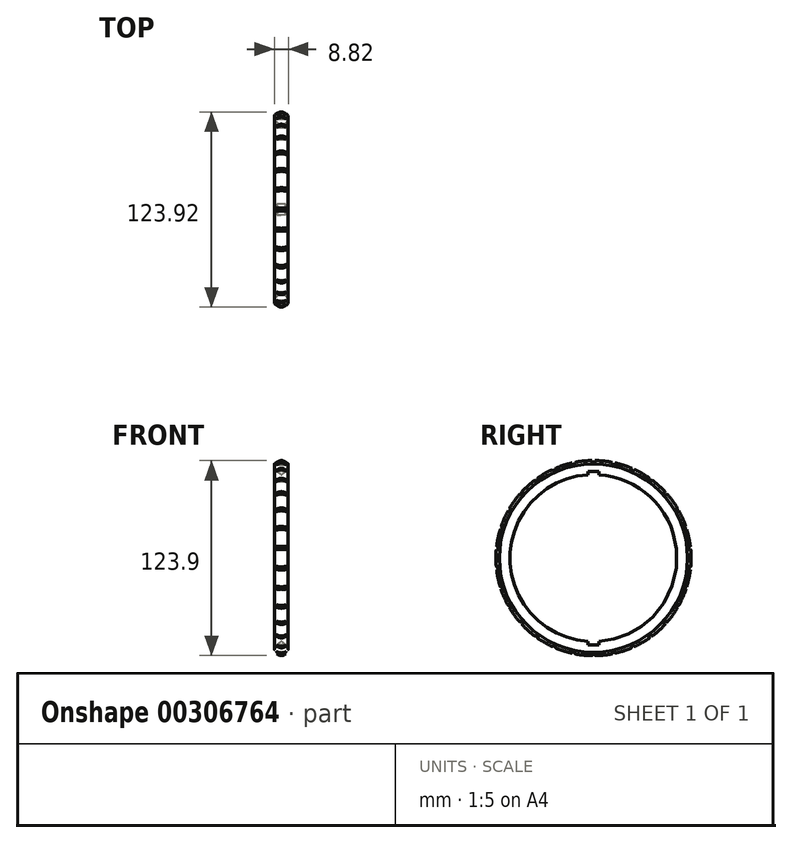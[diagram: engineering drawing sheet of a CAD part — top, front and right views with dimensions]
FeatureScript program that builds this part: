
annotation { "Feature Type Name" : "Feature", "Feature Type Description" : "" }
export const myFeature = defineFeature(function(context is Context, id is Id, definition is map)
    precondition{}
    {
        {
            var Q0;
            Q0=qCreatedBy(makeId("Top.planeOp"),FACE);
            var sketch = newSketch(context, id + "F0", { "sketchPlane" : qUnion([Q0])});
            skLineSegment(sketch, "E0", {"start": v(0, 0) * mm, "end": v(0, -12.81) * mm, "construction": true});
            skLineSegment(sketch, "E1", {"start": v(-4.23, -56.43) * mm, "end": v(-0.32, -53.16) * mm});
            skLineSegment(sketch, "E2", {"start": v(0.32, -53.16) * mm, "end": v(4.23, -56.43) * mm});
            skPoint(sketch, "E3.orphan", {"position": v(-5.08, -57.15) * mm});
            skPoint(sketch, "E4.orphan", {"position": v(5.08, -57.15) * mm});
            skLineSegment(sketch, "E5", {"start": v(-4.4, -56.82) * mm, "end": v(-4.4, -59.82) * mm});
            skLineSegment(sketch, "E6", {"start": v(4.4, -59.82) * mm, "end": v(4.4, -56.82) * mm});
            skPoint(sketch, "E7.visualSharp", {"position": v(-4.4, -56.58) * mm});
            skArc(sketch, "E7.filletArc", {"start": v(-4.23, -56.43) * mm, "mid": v(-4.36, -56.6) * mm, "end": v(-4.4, -56.82) * mm});
            skPoint(sketch, "E8.visualSharp", {"position": v(4.4, -56.58) * mm});
            skArc(sketch, "E8.filletArc", {"start": v(4.4, -56.82) * mm, "mid": v(4.36, -56.6) * mm, "end": v(4.23, -56.43) * mm});
            skPoint(sketch, "E9.visualSharp", {"position": v(0, -52.89) * mm});
            skArc(sketch, "E9.filletArc", {"start": v(0.32, -53.16) * mm, "mid": v(0, -53.04) * mm, "end": v(-0.32, -53.16) * mm});
            skLineSegment(sketch, "E10", {"start": v(0, 0) * mm, "end": v(13.38, 0) * mm, "construction": true});
            skFitSpline(sketch, "E11", {"points": [v(-4.4, -59.82) * mm, v(0, -61.96) * mm, v(4.4, -59.82) * mm], "startDerivative": vector(8.81, -6.43) * mm, "endDerivative": vector(8.81, 6.43) * mm});
            skSolve(sketch);
        }
        {
            var Q0;
            Q0=makeQuery(id+"F0.imprint","IMPRINT",FACE,{"disambiguationData":[TD([[makeQuery(id+"F0.imprint","IMPRINT",EDGE,{"derivedFrom":sQuery(id+"F0.wireOp",EDGE,"E1")}),-1.0]])]});
            var Q1;
            Q1=sQuery(id+"F0.wireOp",EDGE,"E10");
            revolve(context, id + "F1", {"entities" : qUnion([Q0]), "axis" : qUnion([Q1]), "revolveType" : RevolveType.FULL});
        }
        {
            var Q0;
            Q0=qCreatedBy(makeId("Top.planeOp"),FACE);
            var sketch = newSketch(context, id + "F2", { "sketchPlane" : qUnion([Q0])});
            skLineSegment(sketch, "E12.bottom", {"start": v(3.5, 3.5) * mm, "end": v(-3.5, 3.5) * mm});
            skLineSegment(sketch, "E12.top", {"start": v(3.5, -3.5) * mm, "end": v(-3.5, -3.5) * mm});
            skLineSegment(sketch, "E12.left", {"start": v(3.5, 3.5) * mm, "end": v(3.5, -3.5) * mm});
            skLineSegment(sketch, "E12.right", {"start": v(-3.5, 3.5) * mm, "end": v(-3.5, -3.5) * mm});
            skPoint(sketch, "E12.middle", {"position": v(0, 0) * mm});
            skSolve(sketch);
        }
        {
            var Q0;
            Q0 = qSketchRegion(id + "F2", true);
            extrude(context, id + "F3", {"entities" : qUnion([Q0]), "operationType" : NewBodyOperationType.REMOVE, "endBound" : BoundingType.SYMMETRIC, "oppositeDirection" : true, "depth" : 110 * mm});
        }
        {
            var Q0;
            Q0=qCreatedBy(makeId("Right.planeOp"),FACE);
            var sketch = newSketch(context, id + "F4", { "sketchPlane" : qUnion([Q0])});
            skLineSegment(sketch, "E13", {"start": v(0, 60.84) * mm, "end": v(-0.97, 60.84) * mm});
            skLineSegment(sketch, "E14", {"start": v(-0.97, 60.84) * mm, "end": v(-0.97, 62.61) * mm});
            skLineSegment(sketch, "E15", {"start": v(-0.97, 62.61) * mm, "end": v(0, 62.61) * mm});
            skLineSegment(sketch, "E16", {"start": v(0, 62.61) * mm, "end": v(0, 60.46) * mm, "construction": true});
            skLineSegment(sketch, "E17.MirrorCS", {"start": v(0.97, 62.61) * mm, "end": v(0, 62.61) * mm});
            skLineSegment(sketch, "E18.MirrorCS", {"start": v(0.97, 60.84) * mm, "end": v(0.97, 62.61) * mm});
            skLineSegment(sketch, "E19.MirrorCS", {"start": v(0, 60.84) * mm, "end": v(0.97, 60.84) * mm});
            skLineSegment(sketch, "E20.1.0", {"start": v(-12.65, 59.5) * mm, "end": v(-13.6, 59.3) * mm});
            skLineSegment(sketch, "E20.1.1", {"start": v(-11.7, 59.7) * mm, "end": v(-12.07, 61.45) * mm});
            skLineSegment(sketch, "E20.1.2", {"start": v(-12.65, 59.5) * mm, "end": v(-11.7, 59.7) * mm});
            skLineSegment(sketch, "E20.1.3", {"start": v(-12.07, 61.45) * mm, "end": v(-13.02, 61.25) * mm});
            skLineSegment(sketch, "E20.1.4", {"start": v(-13.97, 61.04) * mm, "end": v(-13.02, 61.25) * mm});
            skLineSegment(sketch, "E20.1.5", {"start": v(-13.6, 59.3) * mm, "end": v(-13.97, 61.04) * mm});
            skLineSegment(sketch, "E20.2.0", {"start": v(-24.74, 55.58) * mm, "end": v(-25.63, 55.18) * mm});
            skLineSegment(sketch, "E20.2.1", {"start": v(-23.86, 55.97) * mm, "end": v(-24.58, 57.6) * mm});
            skLineSegment(sketch, "E20.2.2", {"start": v(-24.74, 55.58) * mm, "end": v(-23.86, 55.97) * mm});
            skLineSegment(sketch, "E20.2.3", {"start": v(-24.58, 57.6) * mm, "end": v(-25.47, 57.2) * mm});
            skLineSegment(sketch, "E20.2.4", {"start": v(-26.36, 56.8) * mm, "end": v(-25.47, 57.2) * mm});
            skLineSegment(sketch, "E20.2.5", {"start": v(-25.63, 55.18) * mm, "end": v(-26.36, 56.8) * mm});
            skLineSegment(sketch, "E20.3.0", {"start": v(-35.76, 49.22) * mm, "end": v(-36.55, 48.65) * mm});
            skLineSegment(sketch, "E20.3.1", {"start": v(-34.97, 49.79) * mm, "end": v(-36.02, 51.23) * mm});
            skLineSegment(sketch, "E20.3.2", {"start": v(-35.76, 49.22) * mm, "end": v(-34.97, 49.79) * mm});
            skLineSegment(sketch, "E20.3.3", {"start": v(-36.02, 51.23) * mm, "end": v(-36.8, 50.66) * mm});
            skLineSegment(sketch, "E20.3.4", {"start": v(-37.59, 50.08) * mm, "end": v(-36.8, 50.66) * mm});
            skLineSegment(sketch, "E20.3.5", {"start": v(-36.55, 48.65) * mm, "end": v(-37.59, 50.08) * mm});
            skLineSegment(sketch, "E20.4.0", {"start": v(-45.21, 40.7) * mm, "end": v(-45.86, 39.99) * mm});
            skLineSegment(sketch, "E20.4.1", {"start": v(-44.56, 41.43) * mm, "end": v(-45.88, 42.62) * mm});
            skLineSegment(sketch, "E20.4.2", {"start": v(-45.21, 40.7) * mm, "end": v(-44.56, 41.43) * mm});
            skLineSegment(sketch, "E20.4.3", {"start": v(-45.88, 42.62) * mm, "end": v(-46.53, 41.9) * mm});
            skLineSegment(sketch, "E20.4.4", {"start": v(-47.18, 41.17) * mm, "end": v(-46.53, 41.9) * mm});
            skLineSegment(sketch, "E20.4.5", {"start": v(-45.86, 39.99) * mm, "end": v(-47.18, 41.17) * mm});
            skLineSegment(sketch, "E20.5.0", {"start": v(-52.69, 30.42) * mm, "end": v(-53.17, 29.58) * mm});
            skLineSegment(sketch, "E20.5.1", {"start": v(-52.2, 31.26) * mm, "end": v(-53.74, 32.15) * mm});
            skLineSegment(sketch, "E20.5.2", {"start": v(-52.69, 30.42) * mm, "end": v(-52.2, 31.26) * mm});
            skLineSegment(sketch, "E20.5.3", {"start": v(-53.74, 32.15) * mm, "end": v(-54.22, 31.3) * mm});
            skLineSegment(sketch, "E20.5.4", {"start": v(-54.71, 30.46) * mm, "end": v(-54.22, 31.3) * mm});
            skLineSegment(sketch, "E20.5.5", {"start": v(-53.17, 29.58) * mm, "end": v(-54.71, 30.46) * mm});
            skLineSegment(sketch, "E20.6.0", {"start": v(-57.86, 18.8) * mm, "end": v(-58.16, 17.88) * mm});
            skLineSegment(sketch, "E20.6.1", {"start": v(-57.56, 19.72) * mm, "end": v(-59.25, 20.27) * mm});
            skLineSegment(sketch, "E20.6.2", {"start": v(-57.86, 18.8) * mm, "end": v(-57.56, 19.72) * mm});
            skLineSegment(sketch, "E20.6.3", {"start": v(-59.25, 20.27) * mm, "end": v(-59.55, 19.35) * mm});
            skLineSegment(sketch, "E20.6.4", {"start": v(-59.85, 18.42) * mm, "end": v(-59.55, 19.35) * mm});
            skLineSegment(sketch, "E20.6.5", {"start": v(-58.16, 17.88) * mm, "end": v(-59.85, 18.42) * mm});
            skLineSegment(sketch, "E20.7.0", {"start": v(-60.5, 6.36) * mm, "end": v(-60.6, 5.4) * mm});
            skLineSegment(sketch, "E20.7.1", {"start": v(-60.4, 7.33) * mm, "end": v(-62.17, 7.51) * mm});
            skLineSegment(sketch, "E20.7.2", {"start": v(-60.5, 6.36) * mm, "end": v(-60.4, 7.33) * mm});
            skLineSegment(sketch, "E20.7.3", {"start": v(-62.17, 7.51) * mm, "end": v(-62.27, 6.54) * mm});
            skLineSegment(sketch, "E20.7.4", {"start": v(-62.37, 5.58) * mm, "end": v(-62.27, 6.54) * mm});
            skLineSegment(sketch, "E20.7.5", {"start": v(-60.6, 5.4) * mm, "end": v(-62.37, 5.58) * mm});
            skLineSegment(sketch, "E20.8.0", {"start": v(-60.5, -6.36) * mm, "end": v(-60.4, -7.33) * mm});
            skLineSegment(sketch, "E20.8.1", {"start": v(-60.6, -5.4) * mm, "end": v(-62.37, -5.58) * mm});
            skLineSegment(sketch, "E20.8.2", {"start": v(-60.5, -6.36) * mm, "end": v(-60.6, -5.4) * mm});
            skLineSegment(sketch, "E20.8.3", {"start": v(-62.37, -5.58) * mm, "end": v(-62.27, -6.54) * mm});
            skLineSegment(sketch, "E20.8.4", {"start": v(-62.17, -7.51) * mm, "end": v(-62.27, -6.54) * mm});
            skLineSegment(sketch, "E20.8.5", {"start": v(-60.4, -7.33) * mm, "end": v(-62.17, -7.51) * mm});
            skLineSegment(sketch, "E20.9.0", {"start": v(-57.86, -18.8) * mm, "end": v(-57.56, -19.72) * mm});
            skLineSegment(sketch, "E20.9.1", {"start": v(-58.16, -17.88) * mm, "end": v(-59.85, -18.42) * mm});
            skLineSegment(sketch, "E20.9.2", {"start": v(-57.86, -18.8) * mm, "end": v(-58.16, -17.88) * mm});
            skLineSegment(sketch, "E20.9.3", {"start": v(-59.85, -18.42) * mm, "end": v(-59.55, -19.35) * mm});
            skLineSegment(sketch, "E20.9.4", {"start": v(-59.25, -20.27) * mm, "end": v(-59.55, -19.35) * mm});
            skLineSegment(sketch, "E20.9.5", {"start": v(-57.56, -19.72) * mm, "end": v(-59.25, -20.27) * mm});
            skLineSegment(sketch, "E20.10.0", {"start": v(-52.69, -30.42) * mm, "end": v(-52.2, -31.26) * mm});
            skLineSegment(sketch, "E20.10.1", {"start": v(-53.17, -29.58) * mm, "end": v(-54.71, -30.46) * mm});
            skLineSegment(sketch, "E20.10.2", {"start": v(-52.69, -30.42) * mm, "end": v(-53.17, -29.58) * mm});
            skLineSegment(sketch, "E20.10.3", {"start": v(-54.71, -30.46) * mm, "end": v(-54.22, -31.3) * mm});
            skLineSegment(sketch, "E20.10.4", {"start": v(-53.74, -32.15) * mm, "end": v(-54.22, -31.3) * mm});
            skLineSegment(sketch, "E20.10.5", {"start": v(-52.2, -31.26) * mm, "end": v(-53.74, -32.15) * mm});
            skLineSegment(sketch, "E20.11.0", {"start": v(-45.21, -40.7) * mm, "end": v(-44.56, -41.43) * mm});
            skLineSegment(sketch, "E20.11.1", {"start": v(-45.86, -39.99) * mm, "end": v(-47.18, -41.17) * mm});
            skLineSegment(sketch, "E20.11.2", {"start": v(-45.21, -40.7) * mm, "end": v(-45.86, -39.99) * mm});
            skLineSegment(sketch, "E20.11.3", {"start": v(-47.18, -41.17) * mm, "end": v(-46.53, -41.9) * mm});
            skLineSegment(sketch, "E20.11.4", {"start": v(-45.88, -42.62) * mm, "end": v(-46.53, -41.9) * mm});
            skLineSegment(sketch, "E20.11.5", {"start": v(-44.56, -41.43) * mm, "end": v(-45.88, -42.62) * mm});
            skLineSegment(sketch, "E20.12.0", {"start": v(-35.76, -49.22) * mm, "end": v(-34.97, -49.79) * mm});
            skLineSegment(sketch, "E20.12.1", {"start": v(-36.55, -48.65) * mm, "end": v(-37.59, -50.08) * mm});
            skLineSegment(sketch, "E20.12.2", {"start": v(-35.76, -49.22) * mm, "end": v(-36.55, -48.65) * mm});
            skLineSegment(sketch, "E20.12.3", {"start": v(-37.59, -50.08) * mm, "end": v(-36.8, -50.66) * mm});
            skLineSegment(sketch, "E20.12.4", {"start": v(-36.02, -51.23) * mm, "end": v(-36.8, -50.66) * mm});
            skLineSegment(sketch, "E20.12.5", {"start": v(-34.97, -49.79) * mm, "end": v(-36.02, -51.23) * mm});
            skLineSegment(sketch, "E20.13.0", {"start": v(-24.74, -55.58) * mm, "end": v(-23.86, -55.97) * mm});
            skLineSegment(sketch, "E20.13.1", {"start": v(-25.63, -55.18) * mm, "end": v(-26.36, -56.8) * mm});
            skLineSegment(sketch, "E20.13.2", {"start": v(-24.74, -55.58) * mm, "end": v(-25.63, -55.18) * mm});
            skLineSegment(sketch, "E20.13.3", {"start": v(-26.36, -56.8) * mm, "end": v(-25.47, -57.2) * mm});
            skLineSegment(sketch, "E20.13.4", {"start": v(-24.58, -57.6) * mm, "end": v(-25.47, -57.2) * mm});
            skLineSegment(sketch, "E20.13.5", {"start": v(-23.86, -55.97) * mm, "end": v(-24.58, -57.6) * mm});
            skLineSegment(sketch, "E20.14.0", {"start": v(-12.65, -59.5) * mm, "end": v(-11.7, -59.7) * mm});
            skLineSegment(sketch, "E20.14.1", {"start": v(-13.6, -59.3) * mm, "end": v(-13.97, -61.04) * mm});
            skLineSegment(sketch, "E20.14.2", {"start": v(-12.65, -59.5) * mm, "end": v(-13.6, -59.3) * mm});
            skLineSegment(sketch, "E20.14.3", {"start": v(-13.97, -61.04) * mm, "end": v(-13.02, -61.25) * mm});
            skLineSegment(sketch, "E20.14.4", {"start": v(-12.07, -61.45) * mm, "end": v(-13.02, -61.25) * mm});
            skLineSegment(sketch, "E20.14.5", {"start": v(-11.7, -59.7) * mm, "end": v(-12.07, -61.45) * mm});
            skLineSegment(sketch, "E20.15.0", {"start": v(0, -60.84) * mm, "end": v(0.97, -60.84) * mm});
            skLineSegment(sketch, "E20.15.1", {"start": v(-0.97, -60.84) * mm, "end": v(-0.97, -62.61) * mm});
            skLineSegment(sketch, "E20.15.2", {"start": v(0, -60.84) * mm, "end": v(-0.97, -60.84) * mm});
            skLineSegment(sketch, "E20.15.3", {"start": v(-0.97, -62.61) * mm, "end": v(0, -62.61) * mm});
            skLineSegment(sketch, "E20.15.4", {"start": v(0.97, -62.61) * mm, "end": v(0, -62.61) * mm});
            skLineSegment(sketch, "E20.15.5", {"start": v(0.97, -60.84) * mm, "end": v(0.97, -62.61) * mm});
            skLineSegment(sketch, "E20.16.0", {"start": v(12.65, -59.5) * mm, "end": v(13.6, -59.3) * mm});
            skLineSegment(sketch, "E20.16.1", {"start": v(11.7, -59.7) * mm, "end": v(12.07, -61.45) * mm});
            skLineSegment(sketch, "E20.16.2", {"start": v(12.65, -59.5) * mm, "end": v(11.7, -59.7) * mm});
            skLineSegment(sketch, "E20.16.3", {"start": v(12.07, -61.45) * mm, "end": v(13.02, -61.25) * mm});
            skLineSegment(sketch, "E20.16.4", {"start": v(13.97, -61.04) * mm, "end": v(13.02, -61.25) * mm});
            skLineSegment(sketch, "E20.16.5", {"start": v(13.6, -59.3) * mm, "end": v(13.97, -61.04) * mm});
            skLineSegment(sketch, "E20.17.0", {"start": v(24.74, -55.58) * mm, "end": v(25.63, -55.18) * mm});
            skLineSegment(sketch, "E20.17.1", {"start": v(23.86, -55.97) * mm, "end": v(24.58, -57.6) * mm});
            skLineSegment(sketch, "E20.17.2", {"start": v(24.74, -55.58) * mm, "end": v(23.86, -55.97) * mm});
            skLineSegment(sketch, "E20.17.3", {"start": v(24.58, -57.6) * mm, "end": v(25.47, -57.2) * mm});
            skLineSegment(sketch, "E20.17.4", {"start": v(26.36, -56.8) * mm, "end": v(25.47, -57.2) * mm});
            skLineSegment(sketch, "E20.17.5", {"start": v(25.63, -55.18) * mm, "end": v(26.36, -56.8) * mm});
            skLineSegment(sketch, "E20.18.0", {"start": v(35.76, -49.22) * mm, "end": v(36.55, -48.65) * mm});
            skLineSegment(sketch, "E20.18.1", {"start": v(34.97, -49.79) * mm, "end": v(36.02, -51.23) * mm});
            skLineSegment(sketch, "E20.18.2", {"start": v(35.76, -49.22) * mm, "end": v(34.97, -49.79) * mm});
            skLineSegment(sketch, "E20.18.3", {"start": v(36.02, -51.23) * mm, "end": v(36.8, -50.66) * mm});
            skLineSegment(sketch, "E20.18.4", {"start": v(37.59, -50.08) * mm, "end": v(36.8, -50.66) * mm});
            skLineSegment(sketch, "E20.18.5", {"start": v(36.55, -48.65) * mm, "end": v(37.59, -50.08) * mm});
            skLineSegment(sketch, "E20.19.0", {"start": v(45.21, -40.7) * mm, "end": v(45.86, -39.99) * mm});
            skLineSegment(sketch, "E20.19.1", {"start": v(44.56, -41.43) * mm, "end": v(45.88, -42.62) * mm});
            skLineSegment(sketch, "E20.19.2", {"start": v(45.21, -40.7) * mm, "end": v(44.56, -41.43) * mm});
            skLineSegment(sketch, "E20.19.3", {"start": v(45.88, -42.62) * mm, "end": v(46.53, -41.9) * mm});
            skLineSegment(sketch, "E20.19.4", {"start": v(47.18, -41.17) * mm, "end": v(46.53, -41.9) * mm});
            skLineSegment(sketch, "E20.19.5", {"start": v(45.86, -39.99) * mm, "end": v(47.18, -41.17) * mm});
            skLineSegment(sketch, "E20.20.0", {"start": v(52.69, -30.42) * mm, "end": v(53.17, -29.58) * mm});
            skLineSegment(sketch, "E20.20.1", {"start": v(52.2, -31.26) * mm, "end": v(53.74, -32.15) * mm});
            skLineSegment(sketch, "E20.20.2", {"start": v(52.69, -30.42) * mm, "end": v(52.2, -31.26) * mm});
            skLineSegment(sketch, "E20.20.3", {"start": v(53.74, -32.15) * mm, "end": v(54.22, -31.3) * mm});
            skLineSegment(sketch, "E20.20.4", {"start": v(54.71, -30.46) * mm, "end": v(54.22, -31.3) * mm});
            skLineSegment(sketch, "E20.20.5", {"start": v(53.17, -29.58) * mm, "end": v(54.71, -30.46) * mm});
            skLineSegment(sketch, "E20.21.0", {"start": v(57.86, -18.8) * mm, "end": v(58.16, -17.88) * mm});
            skLineSegment(sketch, "E20.21.1", {"start": v(57.56, -19.72) * mm, "end": v(59.25, -20.27) * mm});
            skLineSegment(sketch, "E20.21.2", {"start": v(57.86, -18.8) * mm, "end": v(57.56, -19.72) * mm});
            skLineSegment(sketch, "E20.21.3", {"start": v(59.25, -20.27) * mm, "end": v(59.55, -19.35) * mm});
            skLineSegment(sketch, "E20.21.4", {"start": v(59.85, -18.42) * mm, "end": v(59.55, -19.35) * mm});
            skLineSegment(sketch, "E20.21.5", {"start": v(58.16, -17.88) * mm, "end": v(59.85, -18.42) * mm});
            skLineSegment(sketch, "E20.22.0", {"start": v(60.5, -6.36) * mm, "end": v(60.6, -5.4) * mm});
            skLineSegment(sketch, "E20.22.1", {"start": v(60.4, -7.33) * mm, "end": v(62.17, -7.51) * mm});
            skLineSegment(sketch, "E20.22.2", {"start": v(60.5, -6.36) * mm, "end": v(60.4, -7.33) * mm});
            skLineSegment(sketch, "E20.22.3", {"start": v(62.17, -7.51) * mm, "end": v(62.27, -6.54) * mm});
            skLineSegment(sketch, "E20.22.4", {"start": v(62.37, -5.58) * mm, "end": v(62.27, -6.54) * mm});
            skLineSegment(sketch, "E20.22.5", {"start": v(60.6, -5.4) * mm, "end": v(62.37, -5.58) * mm});
            skLineSegment(sketch, "E20.23.0", {"start": v(60.5, 6.36) * mm, "end": v(60.4, 7.33) * mm});
            skLineSegment(sketch, "E20.23.1", {"start": v(60.6, 5.4) * mm, "end": v(62.37, 5.58) * mm});
            skLineSegment(sketch, "E20.23.2", {"start": v(60.5, 6.36) * mm, "end": v(60.6, 5.4) * mm});
            skLineSegment(sketch, "E20.23.3", {"start": v(62.37, 5.58) * mm, "end": v(62.27, 6.54) * mm});
            skLineSegment(sketch, "E20.23.4", {"start": v(62.17, 7.51) * mm, "end": v(62.27, 6.54) * mm});
            skLineSegment(sketch, "E20.23.5", {"start": v(60.4, 7.33) * mm, "end": v(62.17, 7.51) * mm});
            skPoint(sketch, "E20.center", {"position": v(0, 0) * mm});
            skLineSegment(sketch, "E21.3.24.0", {"start": v(58.16, 17.88) * mm, "end": v(59.85, 18.42) * mm});
            skLineSegment(sketch, "E21.4.24.0", {"start": v(57.86, 18.8) * mm, "end": v(57.56, 19.72) * mm});
            skLineSegment(sketch, "E21.6.24.0", {"start": v(57.86, 18.8) * mm, "end": v(58.16, 17.88) * mm});
            skLineSegment(sketch, "E21.9.24.0", {"start": v(59.85, 18.42) * mm, "end": v(59.55, 19.35) * mm});
            skLineSegment(sketch, "E21.12.24.0", {"start": v(59.25, 20.27) * mm, "end": v(59.55, 19.35) * mm});
            skLineSegment(sketch, "E21.15.24.0", {"start": v(57.56, 19.72) * mm, "end": v(59.25, 20.27) * mm});
            skLineSegment(sketch, "E21.3.25.0", {"start": v(53.17, 29.58) * mm, "end": v(54.71, 30.46) * mm});
            skLineSegment(sketch, "E21.4.25.0", {"start": v(52.69, 30.42) * mm, "end": v(52.2, 31.26) * mm});
            skLineSegment(sketch, "E21.6.25.0", {"start": v(52.69, 30.42) * mm, "end": v(53.17, 29.58) * mm});
            skLineSegment(sketch, "E21.9.25.0", {"start": v(54.71, 30.46) * mm, "end": v(54.22, 31.3) * mm});
            skLineSegment(sketch, "E21.12.25.0", {"start": v(53.74, 32.15) * mm, "end": v(54.22, 31.3) * mm});
            skLineSegment(sketch, "E21.15.25.0", {"start": v(52.2, 31.26) * mm, "end": v(53.74, 32.15) * mm});
            skLineSegment(sketch, "E21.3.26.0", {"start": v(45.86, 39.99) * mm, "end": v(47.18, 41.17) * mm});
            skLineSegment(sketch, "E21.4.26.0", {"start": v(45.21, 40.7) * mm, "end": v(44.56, 41.43) * mm});
            skLineSegment(sketch, "E21.6.26.0", {"start": v(45.21, 40.7) * mm, "end": v(45.86, 39.99) * mm});
            skLineSegment(sketch, "E21.9.26.0", {"start": v(47.18, 41.17) * mm, "end": v(46.53, 41.9) * mm});
            skLineSegment(sketch, "E21.12.26.0", {"start": v(45.88, 42.62) * mm, "end": v(46.53, 41.9) * mm});
            skLineSegment(sketch, "E21.15.26.0", {"start": v(44.56, 41.43) * mm, "end": v(45.88, 42.62) * mm});
            skLineSegment(sketch, "E21.3.27.0", {"start": v(36.55, 48.65) * mm, "end": v(37.59, 50.08) * mm});
            skLineSegment(sketch, "E21.4.27.0", {"start": v(35.76, 49.22) * mm, "end": v(34.97, 49.79) * mm});
            skLineSegment(sketch, "E21.6.27.0", {"start": v(35.76, 49.22) * mm, "end": v(36.55, 48.65) * mm});
            skLineSegment(sketch, "E21.9.27.0", {"start": v(37.59, 50.08) * mm, "end": v(36.8, 50.66) * mm});
            skLineSegment(sketch, "E21.12.27.0", {"start": v(36.02, 51.23) * mm, "end": v(36.8, 50.66) * mm});
            skLineSegment(sketch, "E21.15.27.0", {"start": v(34.97, 49.79) * mm, "end": v(36.02, 51.23) * mm});
            skLineSegment(sketch, "E21.3.28.0", {"start": v(25.63, 55.18) * mm, "end": v(26.36, 56.8) * mm});
            skLineSegment(sketch, "E21.4.28.0", {"start": v(24.74, 55.58) * mm, "end": v(23.86, 55.97) * mm});
            skLineSegment(sketch, "E21.6.28.0", {"start": v(24.74, 55.58) * mm, "end": v(25.63, 55.18) * mm});
            skLineSegment(sketch, "E21.9.28.0", {"start": v(26.36, 56.8) * mm, "end": v(25.47, 57.2) * mm});
            skLineSegment(sketch, "E21.12.28.0", {"start": v(24.58, 57.6) * mm, "end": v(25.47, 57.2) * mm});
            skLineSegment(sketch, "E21.15.28.0", {"start": v(23.86, 55.97) * mm, "end": v(24.58, 57.6) * mm});
            skLineSegment(sketch, "E21.3.29.0", {"start": v(13.6, 59.3) * mm, "end": v(13.97, 61.04) * mm});
            skLineSegment(sketch, "E21.4.29.0", {"start": v(12.65, 59.5) * mm, "end": v(11.7, 59.7) * mm});
            skLineSegment(sketch, "E21.6.29.0", {"start": v(12.65, 59.5) * mm, "end": v(13.6, 59.3) * mm});
            skLineSegment(sketch, "E21.9.29.0", {"start": v(13.97, 61.04) * mm, "end": v(13.02, 61.25) * mm});
            skLineSegment(sketch, "E21.12.29.0", {"start": v(12.07, 61.45) * mm, "end": v(13.02, 61.25) * mm});
            skLineSegment(sketch, "E21.15.29.0", {"start": v(11.7, 59.7) * mm, "end": v(12.07, 61.45) * mm});
            skSolve(sketch);
        }
        {
            var Q0;
            Q0 = qSketchRegion(id + "F4", true);
            extrude(context, id + "F5", {"entities" : qUnion([Q0]), "operationType" : NewBodyOperationType.REMOVE, "endBound" : BoundingType.SYMMETRIC, "oppositeDirection" : true, "depth" : 25 * mm});
        }
    });
